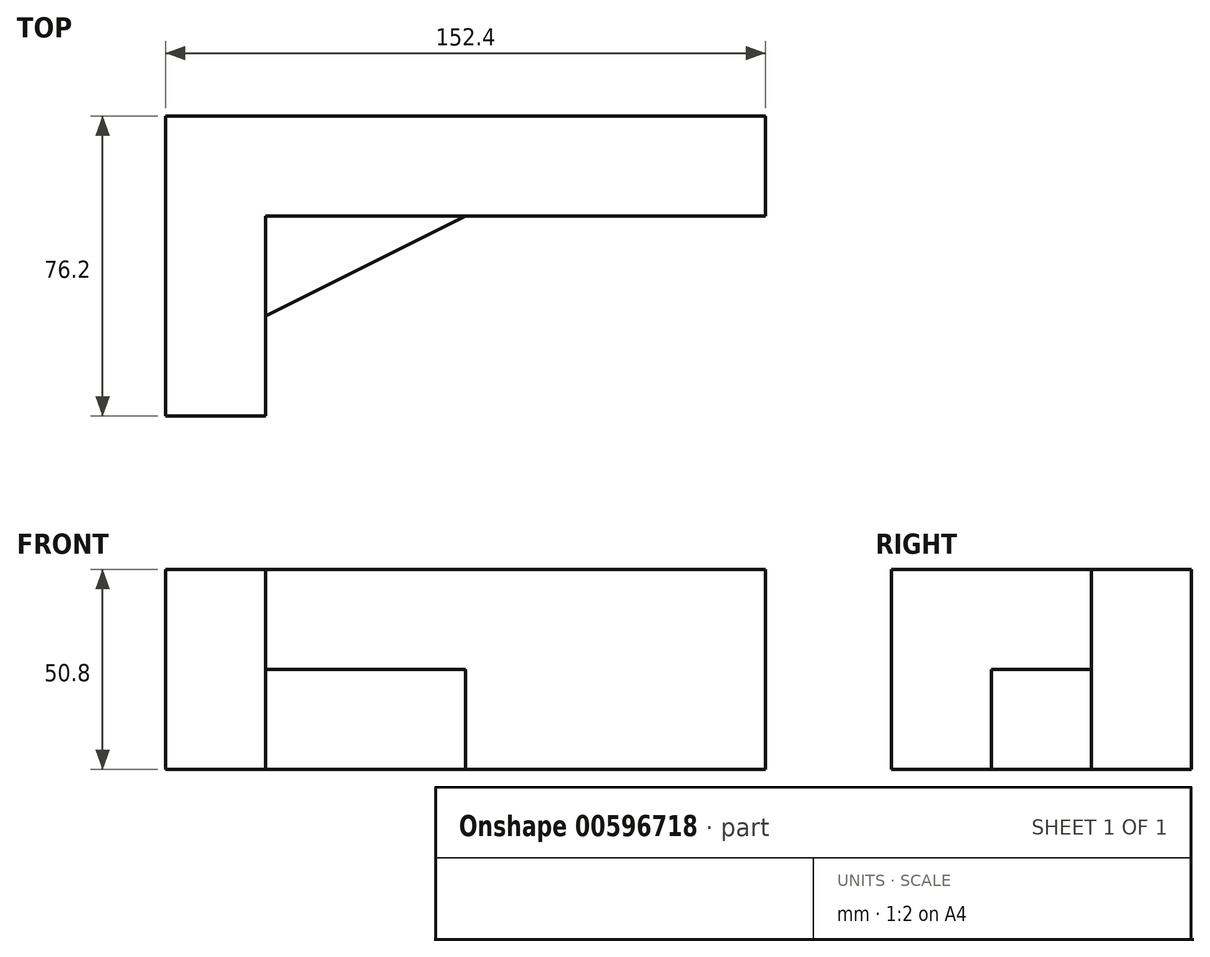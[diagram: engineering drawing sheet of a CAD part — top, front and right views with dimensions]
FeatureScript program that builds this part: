
annotation { "Feature Type Name" : "Feature", "Feature Type Description" : "" }
export const myFeature = defineFeature(function(context is Context, id is Id, definition is map)
    precondition{}
    {
        {
            var Q0;
            Q0=qCreatedBy(makeId("Front.planeOp"),FACE);
            var sketch = newSketch(context, id + "F0", { "sketchPlane" : qUnion([Q0])});
            skLineSegment(sketch, "E0.bottom", {"start": v(0, 0) * mm, "end": v(-152.4, 0) * mm});
            skLineSegment(sketch, "E0.top", {"start": v(0, 50.8) * mm, "end": v(-152.4, 50.8) * mm});
            skLineSegment(sketch, "E0.left", {"start": v(0, 0) * mm, "end": v(0, 50.8) * mm});
            skLineSegment(sketch, "E0.right", {"start": v(-152.4, 0) * mm, "end": v(-152.4, 50.8) * mm});
            skSolve(sketch);
        }
        {
            var Q0;
            Q0=makeQuery(id+"F0.imprint","IMPRINT",FACE,{"disambiguationData":[TD([[makeQuery(id+"F0.imprint","IMPRINT",EDGE,{"derivedFrom":sQuery(id+"F0.wireOp",EDGE,"E0.bottom")}),-1.0]])]});
            extrude(context, id + "F1", {"entities" : qUnion([Q0]), "depth" : 76.2 * mm, "offsetDistance" : 25.4 * mm});
        }
        {
            var Q0;
            Q0=makeQuery(id+"F1.opExtrude","CAP_FACE",FACE,{"disambiguationData":[OSD([sQuery(id+"F0.wireOp",EDGE,"E0.bottom"),sQuery(id+"F0.wireOp",EDGE,"E0.top"),sQuery(id+"F0.wireOp",EDGE,"E0.left"),sQuery(id+"F0.wireOp",EDGE,"E0.right")])],"isStart":false});
            var sketch = newSketch(context, id + "F2", { "sketchPlane" : qUnion([Q0])});
            skLineSegment(sketch, "E1", {"start": v(-152.4, 0) * mm, "end": v(-127, 0) * mm});
            skLineSegment(sketch, "E2", {"start": v(-127, 0) * mm, "end": v(-127, 50.8) * mm});
            skSolve(sketch);
        }
        {
            var Q0;
            {var subQ0=sQuery(id+"F2.wireOp",EDGE,"E2");Q0=makeQuery(id+"F2.imprint","IMPRINT",FACE,{"disambiguationData":[TD([[makeQuery(id+"F2.imprint","IMPRINT",EDGE,{"derivedFrom":subQ0}),-1.0]])]});}
            extrude(context, id + "F3", {"entities" : qUnion([Q0]), "operationType" : NewBodyOperationType.REMOVE, "oppositeDirection" : true, "depth" : 50.8 * mm, "offsetDistance" : 25.4 * mm});
        }
        {
            var Q0;
            Q0=makeQuery(id+"F3.boolean.opBoolean","COPY",FACE,{"derivedFrom":makeQuery(id+"F3.opExtrude","SWEPT_FACE",FACE,{"disambiguationData":[OSD([sQuery(id+"F2.wireOp",EDGE,"E2")])]})});
            var sketch = newSketch(context, id + "F4", { "sketchPlane" : qUnion([Q0])});
            skLineSegment(sketch, "E3.bottom", {"start": v(-25.4, 0) * mm, "end": v(-50.8, 0) * mm});
            skLineSegment(sketch, "E3.top", {"start": v(-25.4, 25.4) * mm, "end": v(-50.8, 25.4) * mm});
            skLineSegment(sketch, "E3.left", {"start": v(-25.4, 0) * mm, "end": v(-25.4, 25.4) * mm});
            skLineSegment(sketch, "E3.right", {"start": v(-50.8, 0) * mm, "end": v(-50.8, 25.4) * mm});
            skSolve(sketch);
        }
        {
            var Q0;
            Q0=makeQuery(id+"F4.imprint","IMPRINT",FACE,{"disambiguationData":[TD([[makeQuery(id+"F4.imprint","IMPRINT",EDGE,{"derivedFrom":sQuery(id+"F4.wireOp",EDGE,"E3.bottom")}),-1.0]])]});
            extrude(context, id + "F5", {"entities" : qUnion([Q0]), "operationType" : NewBodyOperationType.ADD, "depth" : 50.8 * mm, "offsetDistance" : 25.4 * mm});
        }
        {
            var Q0;
            Q0=makeQuery(id+"F5.opExtrude","SWEPT_FACE",FACE,{"disambiguationData":[OSD([sQuery(id+"F4.wireOp",EDGE,"E3.top")])]});
            var sketch = newSketch(context, id + "F6", { "sketchPlane" : qUnion([Q0])});
            skLineSegment(sketch, "E4", {"start": v(-127, -50.8) * mm, "end": v(-76.2, -25.4) * mm});
            skSolve(sketch);
        }
        {
            var Q0;
            Q0=makeQuery(id+"F6.imprint","IMPRINT",FACE,{"disambiguationData":[TD([[makeQuery(id+"F6.imprint","IMPRINT",EDGE,{"derivedFrom":sQuery(id+"F6.wireOp",EDGE,"E4")}),-1.0]])]});
            extrude(context, id + "F7", {"entities" : qUnion([Q0]), "operationType" : NewBodyOperationType.REMOVE, "oppositeDirection" : true, "depth" : 82.8 * mm, "offsetDistance" : 25.4 * mm});
        }
    });
